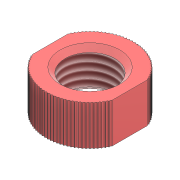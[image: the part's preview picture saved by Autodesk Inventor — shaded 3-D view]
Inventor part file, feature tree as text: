
AUTODESK INVENTOR PART (.ipt)
format: ipt  version: 2022.3 (Build 263350000, 350)  size: 428,032 bytes
history: native  units: mm
features: other x1, extrude x1, chamfer x1, thread x1, sketch x1
ambient origin geometry x8: Origin, YZ Plane, XZ Plane, XY Plane, X Axis, Y Axis, Z Axis, Center Point
bodies: Body1 (feature_tree)
feature tree (5):
  other  "Sólido1"
  extrude  "Extrusión1"  Depth=8.0mm TaperAngle=0.0deg
  chamfer  "Chaflán1"  Distance=1.0mm Angle=45.0deg
  thread  "Rosca1"  [1 undecoded]
  sketch  "Boceto1"  dims[d0=10.0mm d1=8.0mm d2=0.0mm d3=1.0mm d4=2.0mm d5=45.0deg d6=6.2mm d7=0.0mm]
note: 1 required parameter value undecoded (feature->parameter linkage not recoverable at this tier; creation-order binding heuristic only, values carry confidence <= 0.55)
